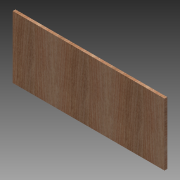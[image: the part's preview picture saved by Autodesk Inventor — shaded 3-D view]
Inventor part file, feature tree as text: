
AUTODESK INVENTOR PART (.ipt)
format: ipt  version: 2013 (Build 170138000, 138)  size: 91,648 bytes
history: native  units: in
note: dims shown in document units (in); Inventor stores cm internally (conversion verified against a paired STEP export)
features: extrude x1, sketch x1
ambient origin geometry x8: Origin, YZ Plane, XZ Plane, XY Plane, X Axis, Y Axis, Z Axis, Center Point
bodies: Solid1 (feature_tree)
feature tree (2):
  extrude  "Extrusion1"  Depth=28.0in
  sketch  "Sketch1"  dims[d0=11.5in d1=28.0in d2=0.5in d3=0.0in]
